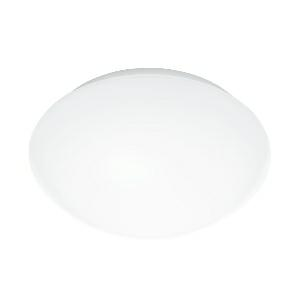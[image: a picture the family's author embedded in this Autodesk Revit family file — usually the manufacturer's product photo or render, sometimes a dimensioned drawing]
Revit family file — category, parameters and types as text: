
# Revit family: rs_pro_led_p1_056063
name_source: partatom
category: Leuchten
revit_build: Autodesk Revit 2016 (Build: 20190508_0715(x64)
units: mm (PartAtom-declared; Revit-internal decimal feet)

## family parameters
Basisbauteil = Fläche
Beim Laden mit Abzugskörper schneiden = Nein
Bemaßung runder Anschluss = Durchmesser verwenden
Gemeinsam genutzt = Nein
Lichtquelle = Nein
Raumberechnungspunkt = Nein
Teiletyp = Normal

## types (1)
- RS PRO LED P1 (1 x , 960 lm, 3000 K)
    Beschreibung = Dimensions (Ø x H): 280 x 110 mm; Mains power supply: 220 – 240 V / 50 – 60 Hz; Sensor Technology: High frequency; Transmitter power: < 1 mW; HF-system: 5,8 GHz; Output: 9,5 W; Interconnection: Yes; Type of interconnection: Master/master; Luminous flux: 960 lm; Colour temperature: 3000 K; Colour variation LED: SDCM3; Colour Rendering Index CRI: 80-89; With lamp: Yes, STEINEL LED system; Lamp: LED cannot be replaced; LED life expectancy (max. °C): 50000 h; Drop in luminous flux in accordance with LM80: L80B10; Base: without; LED cooling system: Passive Thermo Control; With motion detector: Yes; Detection: also through glass, wood and stud walls; Detection angle: 360 °; Angle of aperture: 160 °; Capability of masking out individual segments: Yes; Electronic scalability: Yes; Mechanical scalability: No; Reach, radial: Ø 8 m (50 m²); Reach, tangential: Ø 8 m (50 m²); Continuous light: selectable, 4h; Photo-cell controller: Yes; Twilight setting: 2 – 2000 lx; Time setting: 5 sec – 15 min; Basic light level function: Yes; Basic light level function time: 10/30 min, all night; Soft light start: Yes; Impact resistance: IK03; IP-rating: IP54; Protection class: II; Ambient temperature: 10 – 40 °C; Housing material: Plastic; Cover material: Plastic, opal; Manufacturer's Warranty: 5 years; Settings via: Potentiometers; With remote control: No; Version: warm white; PU1, EAN: 4007841056063
    CIE Flux Codes = 41 70 89 89 100
    Color Rendering = 80-89
    Color Temperature = 3000 K
    Frequency = 50 Hz, 60 Hz
    Height = 0 mm  [stored 0 ft]
    Hersteller = Steinel
    Lamp Light Flux = 960 lm
    Lamp count = 1
    Lampe = 1 x
    Length = 280 mm
    Luminous efficacy = 107 lm/W
    ModVariant = Nein
    Modell = 056063
    Mounting Type = Surface mounted
    Number of Poles = 1
    OnlyDefault = Ja
    Power Factor = 1
    Product Name = RS PRO LED P1
    Product group = Sensor-switched indoor light
    ProductGroupID = 30
    Protection Class = Protection class II
    Protection Degree = IP 54
    RlxData = <blob elided: 62265 chars, md5=d8e25bcd>
    Scheinlast = 9 VA
    Socket = socket
    Standby Power = 0 W
    System Light Flux = 960 lm
    System Power = 9 W
    Typenbild = produkt1_056063.jpg
    Typenkommentare = Product without accessories
    URL = http://relux.com
    VarID = ---
    Voltage = 0 V
    Vorgabe-Ansicht = 1800 mm
    Weight = 0.00 kg
    Width = 0 mm  [stored 0 ft]

note: [stored X ft] marks values corroborated as IEEE doubles in the binary element streams (Revit-internal decimal feet)

## geometry (parser evidence)
native form markers: Blend x4, Sweep x18
no freeform markers — native parametric forms only
